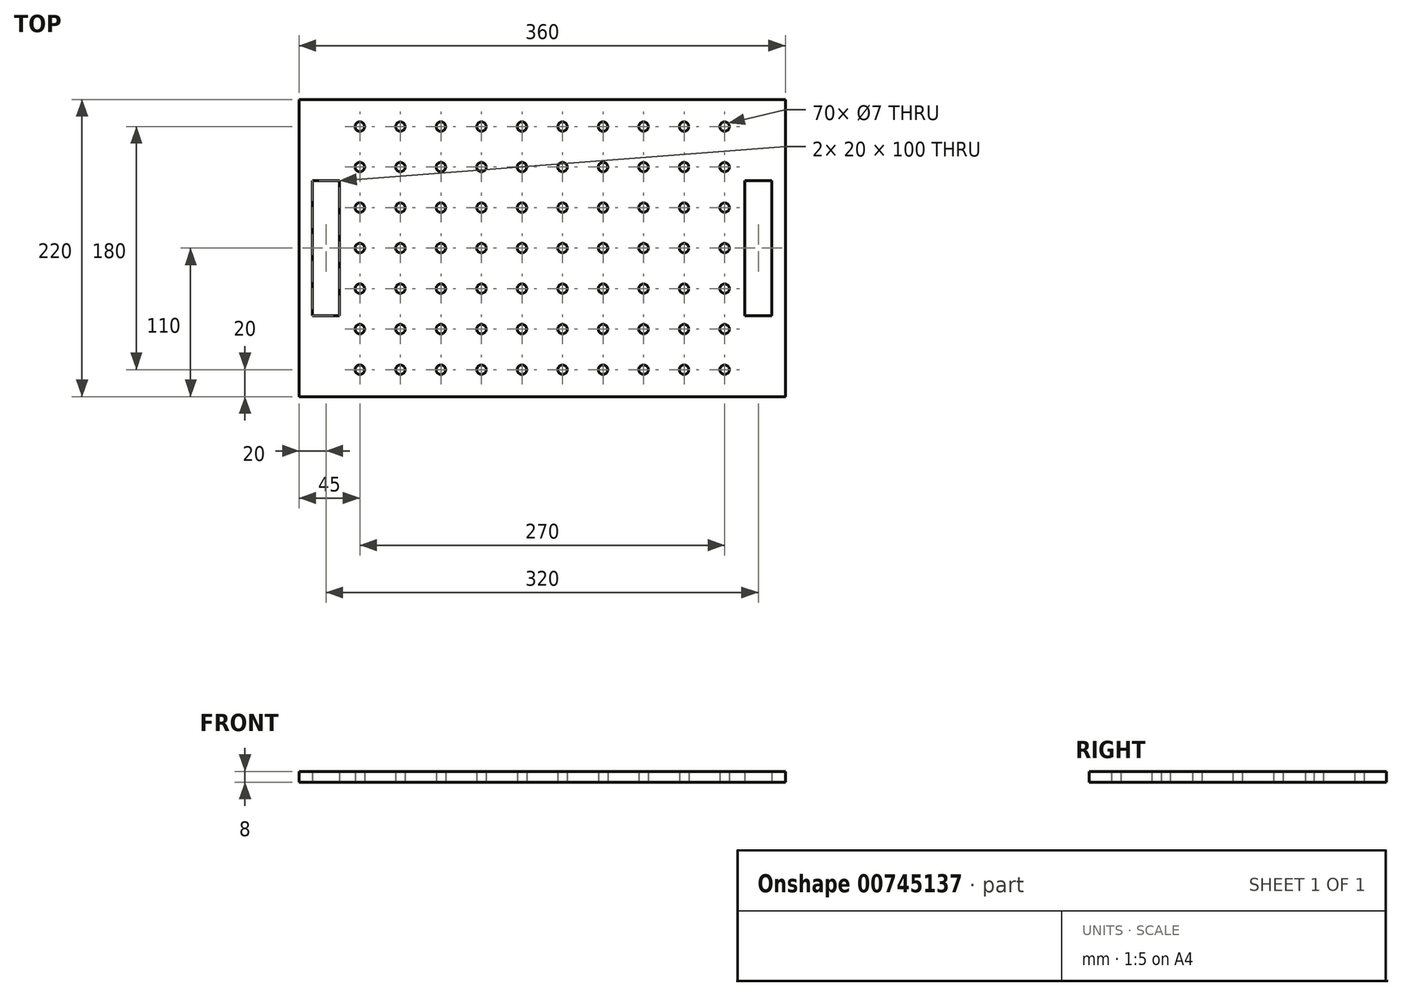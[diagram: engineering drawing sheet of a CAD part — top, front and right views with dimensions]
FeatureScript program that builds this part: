
annotation { "Feature Type Name" : "Feature", "Feature Type Description" : "" }
export const myFeature = defineFeature(function(context is Context, id is Id, definition is map)
    precondition{}
    {
        {
            var Q0;
            Q0=qCreatedBy(makeId("Top.planeOp"),FACE);
            var sketch = newSketch(context, id + "F0", { "sketchPlane" : qUnion([Q0])});
            skLineSegment(sketch, "E0.bottom", {"start": v(180, -110) * mm, "end": v(-180, -110) * mm});
            skLineSegment(sketch, "E0.top", {"start": v(180, 110) * mm, "end": v(-180, 110) * mm});
            skLineSegment(sketch, "E0.left", {"start": v(180, -110) * mm, "end": v(180, 110) * mm});
            skLineSegment(sketch, "E0.right", {"start": v(-180, -110) * mm, "end": v(-180, 110) * mm});
            skPoint(sketch, "E0.middle", {"position": v(0, 0) * mm});
            skLineSegment(sketch, "E1.bottom", {"start": v(170, -50) * mm, "end": v(150, -50) * mm});
            skLineSegment(sketch, "E1.top", {"start": v(170, 50) * mm, "end": v(150, 50) * mm});
            skLineSegment(sketch, "E1.left", {"start": v(170, -50) * mm, "end": v(170, 50) * mm});
            skLineSegment(sketch, "E1.right", {"start": v(150, -50) * mm, "end": v(150, 50) * mm});
            skPoint(sketch, "E1.middle", {"position": v(160, 0) * mm});
            skLineSegment(sketch, "E2.MirrorCS", {"start": v(-170, 50) * mm, "end": v(-150, 50) * mm});
            skLineSegment(sketch, "E3.MirrorCS", {"start": v(-150, -50) * mm, "end": v(-150, 50) * mm});
            skLineSegment(sketch, "E4.MirrorCS", {"start": v(-170, -50) * mm, "end": v(-150, -50) * mm});
            skLineSegment(sketch, "E5.MirrorCS", {"start": v(-170, -50) * mm, "end": v(-170, 50) * mm});
            skCircle(sketch, "E6", {"center": v(135, 90) * mm, "radius": 3.5 * mm});
            skCircle(sketch, "E7.1.0.0", {"center": v(105, 90) * mm, "radius": 3.5 * mm});
            skLineSegment(sketch, "E7.direction1", {"start": v(135, 90) * mm, "end": v(105, 90) * mm, "construction": true});
            skCircle(sketch, "E8.0.2.0", {"center": v(75, 90) * mm, "radius": 3.5 * mm});
            skCircle(sketch, "E8.0.3.0", {"center": v(45, 90) * mm, "radius": 3.5 * mm});
            skCircle(sketch, "E8.0.4.0", {"center": v(15, 90) * mm, "radius": 3.5 * mm});
            skCircle(sketch, "E8.0.5.0", {"center": v(-15, 90) * mm, "radius": 3.5 * mm});
            skCircle(sketch, "E8.0.6.0", {"center": v(-45, 90) * mm, "radius": 3.5 * mm});
            skCircle(sketch, "E8.0.7.0", {"center": v(-75, 90) * mm, "radius": 3.5 * mm});
            skCircle(sketch, "E8.0.8.0", {"center": v(-105, 90) * mm, "radius": 3.5 * mm});
            skCircle(sketch, "E8.0.9.0", {"center": v(-135, 90) * mm, "radius": 3.5 * mm});
            skCircle(sketch, "E9.0.1.0", {"center": v(-135, 60) * mm, "radius": 3.5 * mm});
            skCircle(sketch, "E9.0.1.1", {"center": v(-105, 60) * mm, "radius": 3.5 * mm});
            skCircle(sketch, "E9.0.1.2", {"center": v(-75, 60) * mm, "radius": 3.5 * mm});
            skCircle(sketch, "E9.0.1.3", {"center": v(-45, 60) * mm, "radius": 3.5 * mm});
            skCircle(sketch, "E9.0.1.4", {"center": v(-15, 60) * mm, "radius": 3.5 * mm});
            skCircle(sketch, "E9.0.1.5", {"center": v(15, 60) * mm, "radius": 3.5 * mm});
            skCircle(sketch, "E9.0.1.6", {"center": v(45, 60) * mm, "radius": 3.5 * mm});
            skCircle(sketch, "E9.0.1.7", {"center": v(75, 60) * mm, "radius": 3.5 * mm});
            skCircle(sketch, "E9.0.1.8", {"center": v(105, 60) * mm, "radius": 3.5 * mm});
            skCircle(sketch, "E9.0.1.9", {"center": v(135, 60) * mm, "radius": 3.5 * mm});
            skLineSegment(sketch, "E9.direction1", {"start": v(-135, 90) * mm, "end": v(-105, 90) * mm, "construction": true});
            skLineSegment(sketch, "E9.direction2", {"start": v(-135, 90) * mm, "end": v(-135, 60) * mm, "construction": true});
            skCircle(sketch, "E10.0.0.2", {"center": v(-135, 30) * mm, "radius": 3.5 * mm});
            skCircle(sketch, "E10.2.0.2", {"center": v(-105, 30) * mm, "radius": 3.5 * mm});
            skCircle(sketch, "E10.4.0.2", {"center": v(-75, 30) * mm, "radius": 3.5 * mm});
            skCircle(sketch, "E10.6.0.2", {"center": v(-45, 30) * mm, "radius": 3.5 * mm});
            skCircle(sketch, "E10.8.0.2", {"center": v(-15, 30) * mm, "radius": 3.5 * mm});
            skCircle(sketch, "E10.10.0.2", {"center": v(15, 30) * mm, "radius": 3.5 * mm});
            skCircle(sketch, "E10.12.0.2", {"center": v(45, 30) * mm, "radius": 3.5 * mm});
            skCircle(sketch, "E10.14.0.2", {"center": v(75, 30) * mm, "radius": 3.5 * mm});
            skCircle(sketch, "E10.16.0.2", {"center": v(105, 30) * mm, "radius": 3.5 * mm});
            skCircle(sketch, "E10.18.0.2", {"center": v(135, 30) * mm, "radius": 3.5 * mm});
            skCircle(sketch, "E10.0.0.3", {"center": v(-135, 0) * mm, "radius": 3.5 * mm});
            skCircle(sketch, "E10.2.0.3", {"center": v(-105, 0) * mm, "radius": 3.5 * mm});
            skCircle(sketch, "E10.4.0.3", {"center": v(-75, 0) * mm, "radius": 3.5 * mm});
            skCircle(sketch, "E10.6.0.3", {"center": v(-45, 0) * mm, "radius": 3.5 * mm});
            skCircle(sketch, "E10.8.0.3", {"center": v(-15, 0) * mm, "radius": 3.5 * mm});
            skCircle(sketch, "E10.10.0.3", {"center": v(15, 0) * mm, "radius": 3.5 * mm});
            skCircle(sketch, "E10.12.0.3", {"center": v(45, 0) * mm, "radius": 3.5 * mm});
            skCircle(sketch, "E10.14.0.3", {"center": v(75, 0) * mm, "radius": 3.5 * mm});
            skCircle(sketch, "E10.16.0.3", {"center": v(105, 0) * mm, "radius": 3.5 * mm});
            skCircle(sketch, "E10.18.0.3", {"center": v(135, 0) * mm, "radius": 3.5 * mm});
            skCircle(sketch, "E10.0.0.4", {"center": v(-135, -30) * mm, "radius": 3.5 * mm});
            skCircle(sketch, "E10.2.0.4", {"center": v(-105, -30) * mm, "radius": 3.5 * mm});
            skCircle(sketch, "E10.4.0.4", {"center": v(-75, -30) * mm, "radius": 3.5 * mm});
            skCircle(sketch, "E10.6.0.4", {"center": v(-45, -30) * mm, "radius": 3.5 * mm});
            skCircle(sketch, "E10.8.0.4", {"center": v(-15, -30) * mm, "radius": 3.5 * mm});
            skCircle(sketch, "E10.10.0.4", {"center": v(15, -30) * mm, "radius": 3.5 * mm});
            skCircle(sketch, "E10.12.0.4", {"center": v(45, -30) * mm, "radius": 3.5 * mm});
            skCircle(sketch, "E10.14.0.4", {"center": v(75, -30) * mm, "radius": 3.5 * mm});
            skCircle(sketch, "E10.16.0.4", {"center": v(105, -30) * mm, "radius": 3.5 * mm});
            skCircle(sketch, "E10.18.0.4", {"center": v(135, -30) * mm, "radius": 3.5 * mm});
            skCircle(sketch, "E10.0.0.5", {"center": v(-135, -60) * mm, "radius": 3.5 * mm});
            skCircle(sketch, "E10.2.0.5", {"center": v(-105, -60) * mm, "radius": 3.5 * mm});
            skCircle(sketch, "E10.4.0.5", {"center": v(-75, -60) * mm, "radius": 3.5 * mm});
            skCircle(sketch, "E10.6.0.5", {"center": v(-45, -60) * mm, "radius": 3.5 * mm});
            skCircle(sketch, "E10.8.0.5", {"center": v(-15, -60) * mm, "radius": 3.5 * mm});
            skCircle(sketch, "E10.10.0.5", {"center": v(15, -60) * mm, "radius": 3.5 * mm});
            skCircle(sketch, "E10.12.0.5", {"center": v(45, -60) * mm, "radius": 3.5 * mm});
            skCircle(sketch, "E10.14.0.5", {"center": v(75, -60) * mm, "radius": 3.5 * mm});
            skCircle(sketch, "E10.16.0.5", {"center": v(105, -60) * mm, "radius": 3.5 * mm});
            skCircle(sketch, "E10.18.0.5", {"center": v(135, -60) * mm, "radius": 3.5 * mm});
            skCircle(sketch, "E10.0.0.6", {"center": v(-135, -90) * mm, "radius": 3.5 * mm});
            skCircle(sketch, "E10.2.0.6", {"center": v(-105, -90) * mm, "radius": 3.5 * mm});
            skCircle(sketch, "E10.4.0.6", {"center": v(-75, -90) * mm, "radius": 3.5 * mm});
            skCircle(sketch, "E10.6.0.6", {"center": v(-45, -90) * mm, "radius": 3.5 * mm});
            skCircle(sketch, "E10.8.0.6", {"center": v(-15, -90) * mm, "radius": 3.5 * mm});
            skCircle(sketch, "E10.10.0.6", {"center": v(15, -90) * mm, "radius": 3.5 * mm});
            skCircle(sketch, "E10.12.0.6", {"center": v(45, -90) * mm, "radius": 3.5 * mm});
            skCircle(sketch, "E10.14.0.6", {"center": v(75, -90) * mm, "radius": 3.5 * mm});
            skCircle(sketch, "E10.16.0.6", {"center": v(105, -90) * mm, "radius": 3.5 * mm});
            skCircle(sketch, "E10.18.0.6", {"center": v(135, -90) * mm, "radius": 3.5 * mm});
            skSolve(sketch);
        }
        {
            var Q0;
            Q0=makeQuery(id+"F0.imprint","IMPRINT",FACE,{"disambiguationData":[TD([[makeQuery(id+"F0.imprint","IMPRINT",EDGE,{"derivedFrom":sQuery(id+"F0.wireOp",EDGE,"E0.bottom")}),-1.0]])]});
            extrude(context, id + "F1", {"entities" : qUnion([Q0]), "depth" : 8 * mm, "offsetDistance" : 25 * mm});
        }
    });
